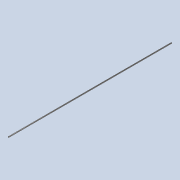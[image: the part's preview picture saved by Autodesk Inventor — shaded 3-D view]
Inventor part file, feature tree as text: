
AUTODESK INVENTOR PART (.ipt)
format: ipt  version: 2021 (Build 250183000, 183)  size: 79,872 bytes
history: native  units: in
note: dims shown in document units (in); Inventor stores cm internally (conversion verified against a paired STEP export)
features: extrude x1, sketch x1
ambient origin geometry x8: Origin, YZ Plane, XZ Plane, XY Plane, X Axis, Y Axis, Z Axis, Center Point
bodies: Solid1 (feature_tree)
feature tree (2):
  extrude  "Extrusion1"  Depth=18.25in TaperAngle=0.0deg
  sketch  "Sketch1"  dims[d0=0.0625in d1=18.25in d2=0.0in]
